# Revit family: Hydrablock C Energy Solar
name_source: partatom
category: Attrezzatura meccanica
units: mm (PartAtom-declared; Revit-internal decimal feet)

## family parameters
Basato su piano di lavoro = No
Classificazione = Nessuno
Condiviso = No
Mantieni orientamento annotazione = No
Punto di calcolo locali = No
Quota connettore circolare = Usa diametro
Sempre verticale = Sì
Taglio con vuoti quando caricato = No
Tipo di parte = Normale

## types (3) — shared parameters
Boiler capacity = 200 Lt.
Date of publishing = 07/01/2025
Depth = 418 mm  [stored 1.37139 ft]
Design country = Italy
Domestic Cold Water Diameter = 26 mm
Domestic Hot Water Diameter = 26 mm
Expansion vassel = 12 Lt.
Expansion vessel temperature renge = -10°C/+100°C
Heat pump delivery = 34 mm
Heat pump return = 34 mm
Height = 2242 mm  [stored 7.35564 ft]
Hydronic Return Diameter = 34 mm
Hydronic Supply Diameter = 34 mm
Manufacturer country = Italy
Manufacturer name = Italtherm S.p.A.
Material main = Metal
Material secondary = Plastic
Maximum boiler pressure = 8 bar
Maximum boiler temperature = 90°C
Maximum vassel pressure = 10 bar
Minimum boiler pressure = 1,5 bar
Mnimum boiler temperature = 5°C
Power supply | Frequency (Hz) = 50 Hz
Power supply | Phase = 1
Power supply | Voltage (V) = 230 V
Product family = Heating
Product group = Thermal unit
Solar attack = 26 mm
Weight = 87,00 kg
Width = 1000 mm  [stored 3.28084 ft]
zero-valued in all types: Prospetto di default

## per-type parameters (varying)
| type | Power consumption (W) | Sound power |
| Hydrablock C Energy 5M Solar | 2840 W | 60 dB |
| Hydrablock C Energy 7M Solar | 3050 W | 63 dB |
| Hydrablock C Energy 9M Solar | 3400 W | 65 dB |

note: [stored X ft] marks values corroborated as IEEE doubles in the binary element streams (Revit-internal decimal feet)
